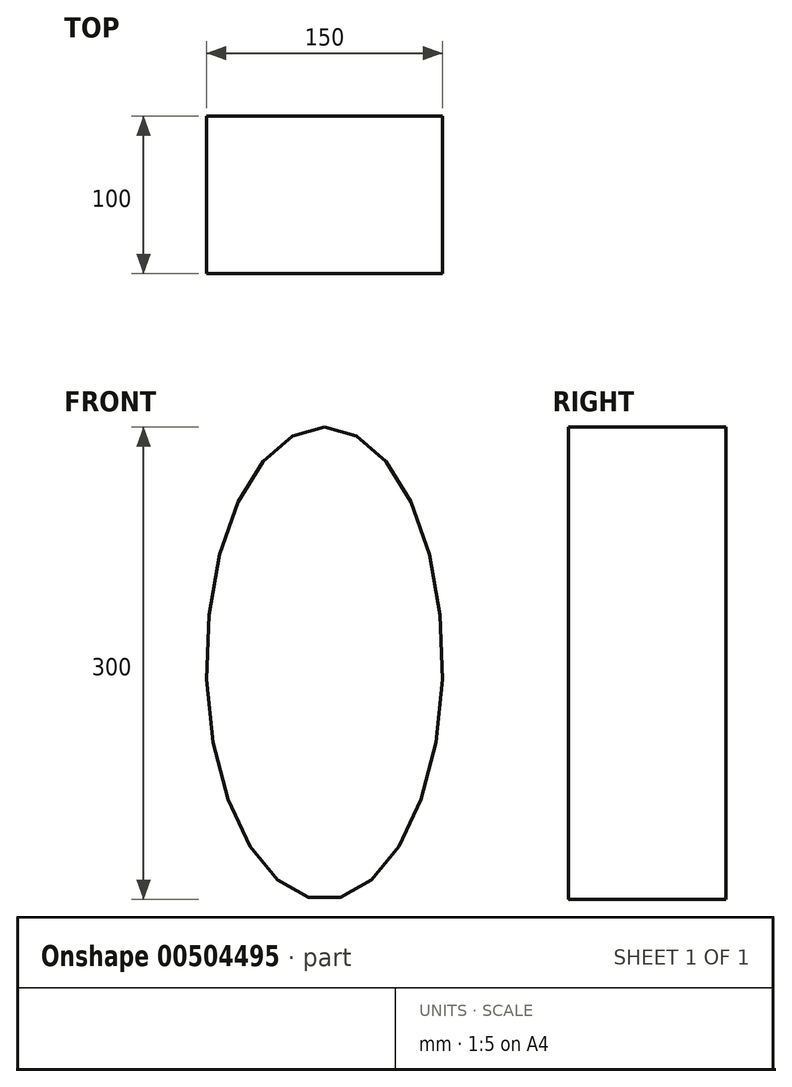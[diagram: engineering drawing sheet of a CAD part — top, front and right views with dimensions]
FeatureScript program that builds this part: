
annotation { "Feature Type Name" : "Feature", "Feature Type Description" : "" }
export const myFeature = defineFeature(function(context is Context, id is Id, definition is map)
    precondition{}
    {
        {
            var Q0;
            Q0=qCreatedBy(makeId("Front.planeOp"),FACE);
            var sketch = newSketch(context, id + "F0", { "sketchPlane" : qUnion([Q0])});
            skEllipse(sketch, "E0", {"center": v(0, 0) * mm, "majorRadius": 150 * mm, "minorRadius": 75 * mm, "majorAxis": v(0, 1)});
            skSolve(sketch);
        }
        {
            var Q0;
            Q0=qCreatedBy(makeId("Front.planeOp"),FACE);
            var sketch = newSketch(context, id + "F1", { "sketchPlane" : qUnion([Q0])});
            skFitSpline(sketch, "E1.0", {"points": [v(3.92, 151.87) * mm, v(0, 152.07) * mm, v(-3.92, 151.87) * mm, v(-9.1, 151.1) * mm, v(-15.48, 149.19) * mm, v(-22.9, 145.45) * mm, v(-30.03, 140.34) * mm, v(-36.84, 133.9) * mm, v(-42.2, 127.49) * mm, v(-46.3, 121.74) * mm, v(-49.26, 117.12) * mm, v(-51.63, 113.03) * mm, v(-53.48, 109.6) * mm, v(-54.83, 106.97) * mm, v(-56.15, 104.27) * mm, v(-57.85, 100.6) * mm, v(-59.9, 95.86) * mm, v(-62.18, 89.97) * mm, v(-65.04, 81.86) * mm, v(-68.2, 71.26) * mm, v(-71.36, 57.9) * mm, v(-73.85, 44) * mm, v(-75.35, 32.05) * mm, v(-76.2, 22.31) * mm, v(-76.66, 14.94) * mm, v(-76.9, 8.74) * mm, v(-76.98, 3.75) * mm, v(-77, 0) * mm, v(-76.98, -3.75) * mm, v(-76.9, -8.74) * mm, v(-76.66, -14.94) * mm, v(-76.2, -22.31) * mm, v(-75.35, -32.05) * mm, v(-73.85, -44) * mm, v(-71.36, -57.9) * mm, v(-68.2, -71.26) * mm, v(-65.04, -81.86) * mm, v(-62.18, -89.97) * mm, v(-59.9, -95.86) * mm, v(-57.85, -100.6) * mm, v(-56.15, -104.27) * mm, v(-54.83, -106.97) * mm, v(-53.48, -109.6) * mm, v(-51.63, -113.03) * mm, v(-49.26, -117.12) * mm, v(-46.3, -121.74) * mm, v(-42.2, -127.49) * mm, v(-36.84, -133.9) * mm, v(-30.03, -140.34) * mm, v(-22.9, -145.45) * mm, v(-15.48, -149.19) * mm, v(-9.1, -151.1) * mm, v(-3.92, -151.87) * mm, v(0, -152.07) * mm, v(3.92, -151.87) * mm, v(9.1, -151.1) * mm, v(15.48, -149.19) * mm, v(22.9, -145.45) * mm, v(30.03, -140.34) * mm, v(36.84, -133.9) * mm, v(42.2, -127.49) * mm, v(46.3, -121.74) * mm, v(49.26, -117.12) * mm, v(51.63, -113.03) * mm, v(53.48, -109.6) * mm, v(54.83, -106.97) * mm, v(56.15, -104.27) * mm, v(57.85, -100.6) * mm, v(59.9, -95.86) * mm, v(62.18, -89.97) * mm, v(65.04, -81.86) * mm, v(68.2, -71.26) * mm, v(71.36, -57.9) * mm, v(73.85, -44) * mm, v(75.35, -32.05) * mm, v(76.2, -22.31) * mm, v(76.66, -14.94) * mm, v(76.9, -8.74) * mm, v(76.98, -3.75) * mm, v(77, 0) * mm, v(76.98, 3.75) * mm, v(76.9, 8.74) * mm, v(76.66, 14.94) * mm, v(76.2, 22.31) * mm, v(75.35, 32.05) * mm, v(73.85, 44) * mm, v(71.36, 57.9) * mm, v(68.2, 71.26) * mm, v(65.04, 81.86) * mm, v(62.18, 89.97) * mm, v(59.9, 95.86) * mm, v(57.85, 100.6) * mm, v(56.15, 104.27) * mm, v(54.83, 106.97) * mm, v(53.48, 109.6) * mm, v(51.63, 113.03) * mm, v(49.26, 117.12) * mm, v(46.3, 121.74) * mm, v(42.2, 127.49) * mm, v(36.84, 133.9) * mm, v(30.03, 140.34) * mm, v(22.9, 145.45) * mm, v(15.48, 149.19) * mm, v(9.1, 151.1) * mm, v(3.92, 151.87) * mm, v(0, 152.07) * mm, v(-3.92, 151.87) * mm, v(3.92, 151.87) * mm]});
            skSolve(sketch);
        }
        {
            var Q0;
            Q0=makeQuery(id+"F0.imprint","IMPRINT",FACE,{"disambiguationData":[TD([[makeQuery(id+"F0.imprint","IMPRINT",EDGE,{"derivedFrom":sQuery(id+"F0.wireOp",EDGE,"E0")}),1.0]])]});
            var Q1;
            Q1=makeQuery(id+"F1.imprint","IMPRINT",FACE,{"disambiguationData":[TD([[makeQuery(id+"F1.imprint","IMPRINT",EDGE,{"derivedFrom":sQuery(id+"F1.wireOp",EDGE,"E1.0")}),1.0]])]});
            extrude(context, id + "F2", {"entities" : qUnion([Q0, Q1]), "depth" : 100 * mm});
        }
    });
